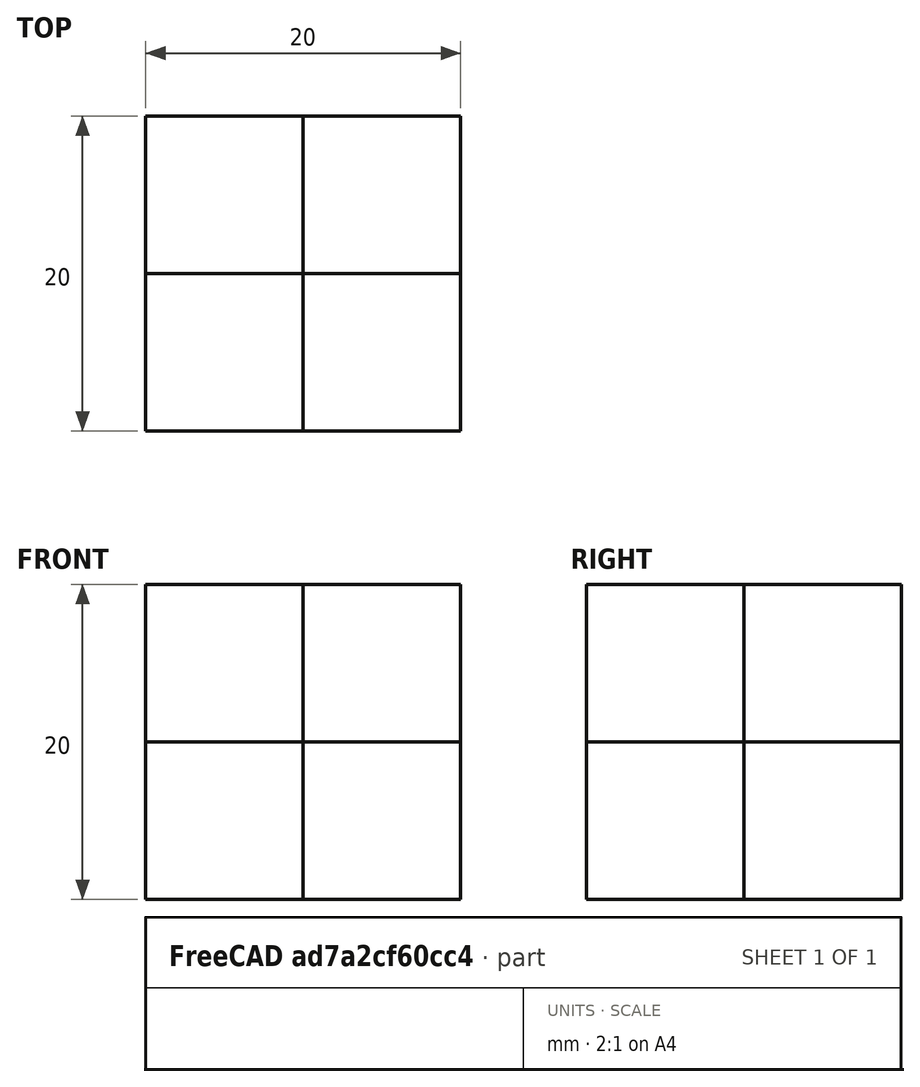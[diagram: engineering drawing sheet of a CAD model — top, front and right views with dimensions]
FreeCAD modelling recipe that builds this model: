
FCSTD DOCUMENT  (FreeCAD 0.16R6706 (Git))
Label: volume and sizes
License: All rights reserved
LicenseURL: http://en.wikipedia.org/wiki/All_rights_reserved
objects: Part::Box×8
note: 8 computed .brp shape members not serialized (recipe doc carries the construction recipe); baked Part::Feature solids carry a one-line shape summary decoded from their .brp

FEATURE [Part::Box] Box  label="Cube"
  Height = 10
  Length = 10
  Width = 10
FEATURE [Part::Box] Box001  label="Cube001"
  Height = 10
  Length = 10
  Placement = pos=(10,0,0) rot=(0,0,1;0rad)
  Width = 10
FEATURE [Part::Box] Box002  label="Cube002"
  Height = 10
  Length = 10
  Placement = pos=(10,10,0) rot=(0,0,1;0rad)
  Width = 10
FEATURE [Part::Box] Box003  label="Cube003"
  Height = 10
  Length = 10
  Placement = pos=(0,10,0) rot=(0,0,1;0rad)
  Width = 10
FEATURE [Part::Box] Box004  label="Cube004"
  Height = 10
  Length = 10
  Placement = pos=(0,0,10) rot=(0,0,1;0rad)
  Width = 10
FEATURE [Part::Box] Box005  label="Cube005"
  Height = 10
  Length = 10
  Placement = pos=(10,0,10) rot=(0,0,1;0rad)
  Width = 10
FEATURE [Part::Box] Box006  label="Cube006"
  Height = 10
  Length = 10
  Placement = pos=(0,10,10) rot=(0,0,1;0rad)
  Width = 10
FEATURE [Part::Box] Box007  label="Cube007"
  Height = 10
  Length = 10
  Placement = pos=(10,10,10) rot=(0,0,1;0rad)
  Width = 10
